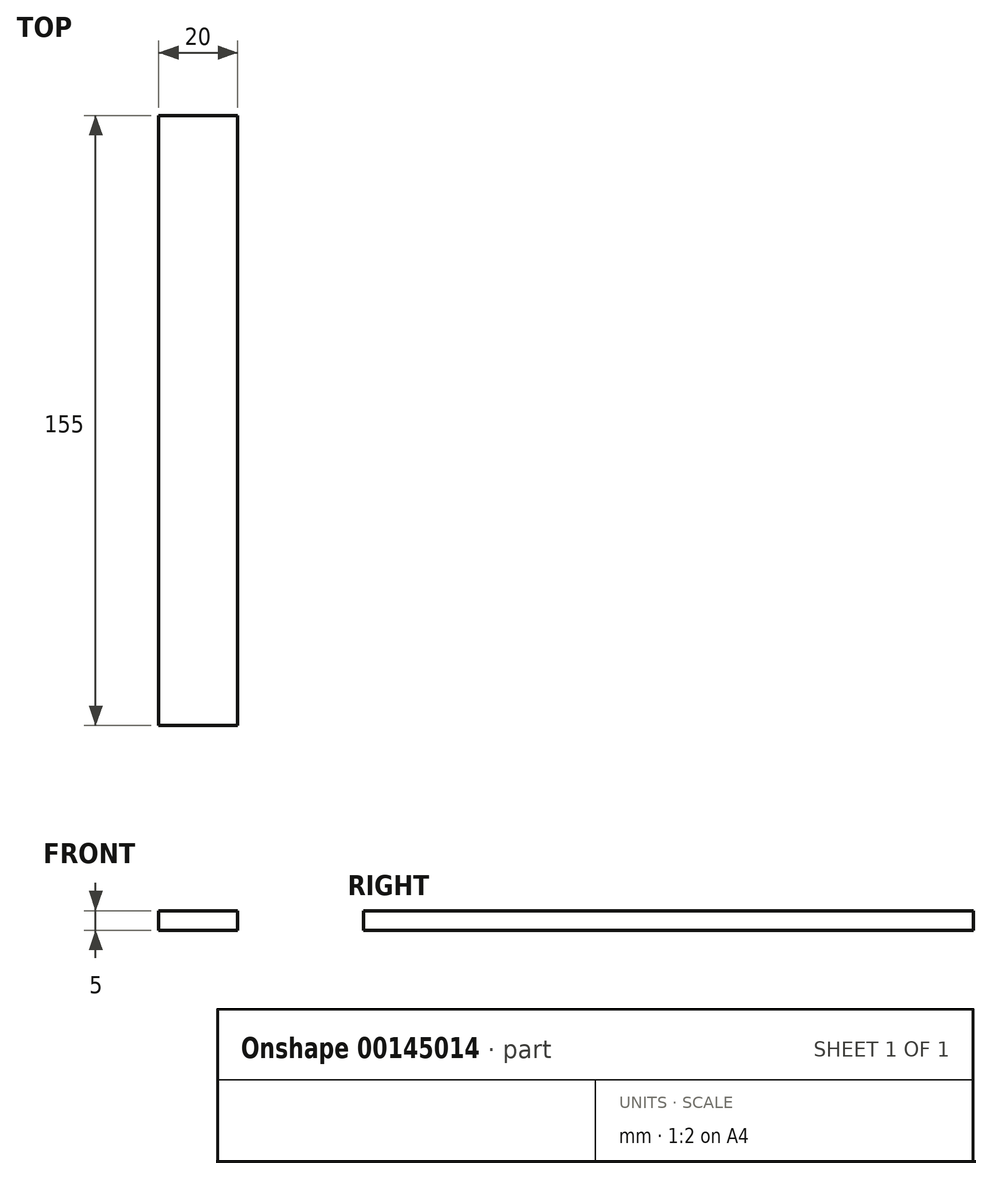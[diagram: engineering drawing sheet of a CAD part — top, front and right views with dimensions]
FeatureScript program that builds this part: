
annotation { "Feature Type Name" : "Feature", "Feature Type Description" : "" }
export const myFeature = defineFeature(function(context is Context, id is Id, definition is map)
    precondition{}
    {
        {
            var Q0;
            Q0=qCreatedBy(makeId("Top.planeOp"),FACE);
            var sketch = newSketch(context, id + "F0", { "sketchPlane" : qUnion([Q0])});
            skLineSegment(sketch, "E0.bottom", {"start": v(8.23, -77.5) * mm, "end": v(-11.77, -77.5) * mm});
            skLineSegment(sketch, "E0.top", {"start": v(8.23, 77.5) * mm, "end": v(-11.77, 77.5) * mm});
            skLineSegment(sketch, "E0.left", {"start": v(8.23, -77.5) * mm, "end": v(8.23, 77.5) * mm});
            skLineSegment(sketch, "E0.right", {"start": v(-11.77, -77.5) * mm, "end": v(-11.77, 77.5) * mm});
            skPoint(sketch, "E0.middle", {"position": v(-1.77, 0) * mm});
            skSolve(sketch);
        }
        {
            var Q0;
            Q0 = qSketchRegion(id + "F0", true);
            extrude(context, id + "F1", {"entities" : qUnion([Q0]), "depth" : 5 * mm});
        }
    });
